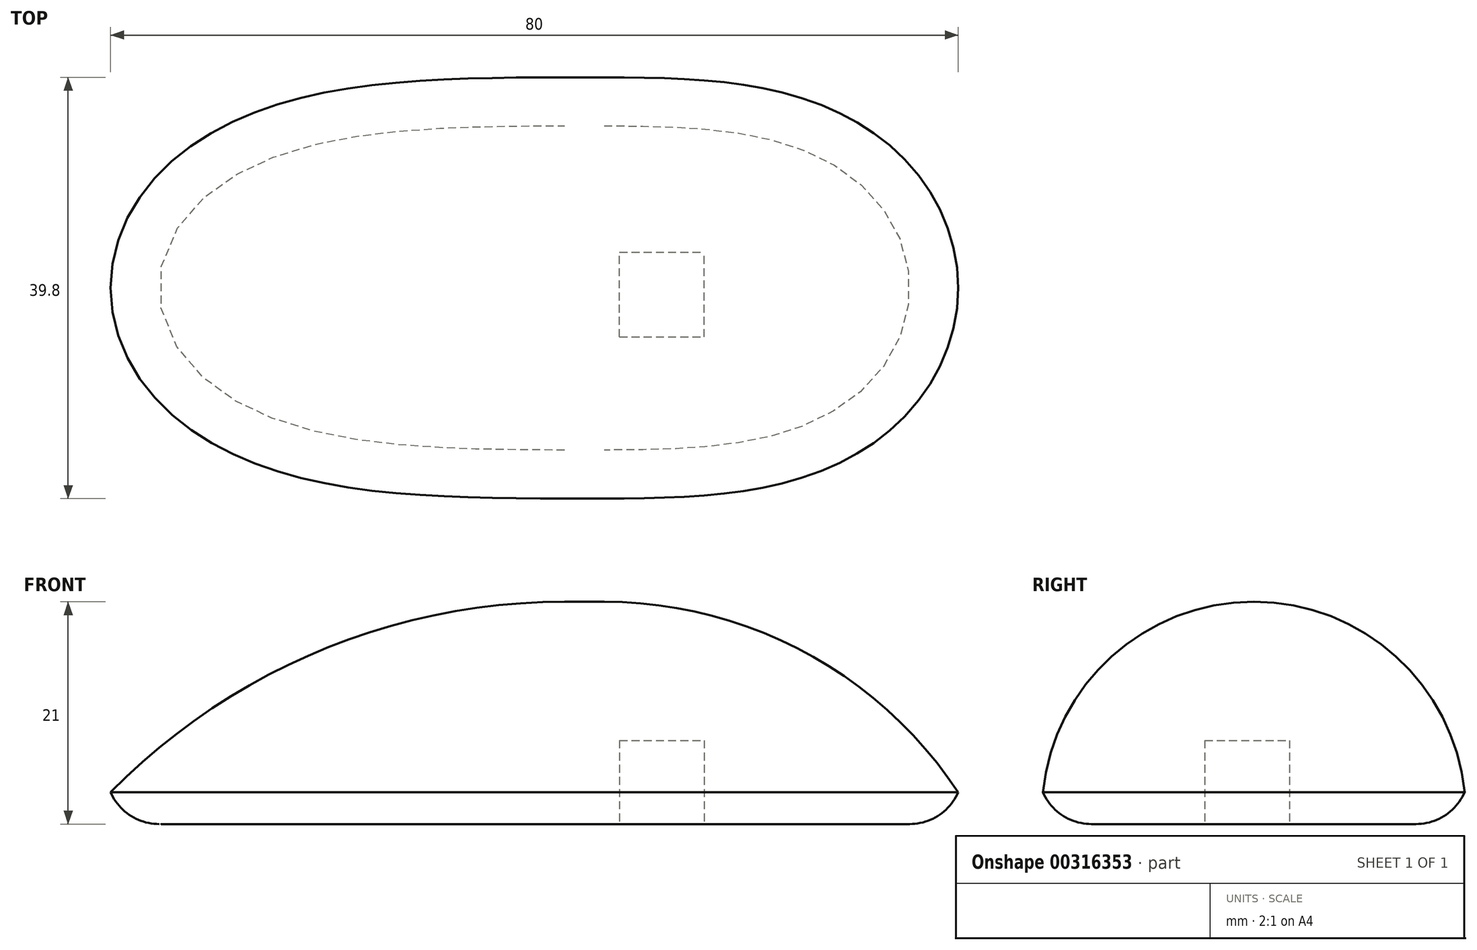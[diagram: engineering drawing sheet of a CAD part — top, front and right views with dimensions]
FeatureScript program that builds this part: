
annotation { "Feature Type Name" : "Feature", "Feature Type Description" : "" }
export const myFeature = defineFeature(function(context is Context, id is Id, definition is map)
    precondition{}
    {
        {
            var Q0;
            Q0=qCreatedBy(makeId("Front.planeOp"),FACE);
            var sketch = newSketch(context, id + "F0", { "sketchPlane" : qUnion([Q0])});
            skLineSegment(sketch, "E0.bottom", {"start": v(-60.2, 40.82) * mm, "end": v(19.8, 40.82) * mm});
            skLineSegment(sketch, "E0.top", {"start": v(-60.2, 22.82) * mm, "end": v(19.8, 22.82) * mm});
            skLineSegment(sketch, "E0.left", {"start": v(-60.2, 40.82) * mm, "end": v(-60.2, 22.82) * mm});
            skLineSegment(sketch, "E0.right", {"start": v(19.8, 40.82) * mm, "end": v(19.8, 22.82) * mm});
            skSolve(sketch);
        }
        {
            var Q0;
            Q0=makeQuery(id+"F0.imprint","IMPRINT",FACE,{"disambiguationData":[TD([[makeQuery(id+"F0.imprint","IMPRINT",EDGE,{"derivedFrom":sQuery(id+"F0.wireOp",EDGE,"E0.bottom")}),-1.0]])]});
            extrude(context, id + "F1", {"entities" : qUnion([Q0]), "depth" : 40 * mm});
        }
        {
            var Q0;
            Q0=makeQuery(id+"F1.opExtrude","SWEPT_EDGE",EDGE,{"disambiguationData":[OSD([sQuery(id+"F0.wireOp",EDGE,"E0.bottom"),sQuery(id+"F0.wireOp",EDGE,"E0.left")])]});
            fillet(context, id + "F2", {"entities" : qUnion([Q0]), "radius" : 60 * mm, "tangentPropagation" : true, "allowEdgeOverflow" : false});
        }
        {
            var Q0;
            Q0=makeQuery(id+"F1.opExtrude","SWEPT_EDGE",EDGE,{"disambiguationData":[OSD([sQuery(id+"F0.wireOp",EDGE,"E0.bottom"),sQuery(id+"F0.wireOp",EDGE,"E0.right")])]});
            fillet(context, id + "F3", {"entities" : qUnion([Q0]), "radius" : 40 * mm, "tangentPropagation" : true, "allowEdgeOverflow" : false});
        }
        {
            var Q0;
            {var subQ0=sQuery(id+"F0.wireOp",EDGE,"E0.left");var subQ1=sQuery(id+"F0.wireOp",EDGE,"E0.bottom");Q0=makeQuery(id+"F2.opFillet","BLEND_EDGE",EDGE,{"blendedFrom":[makeQuery(id+"F1.opExtrude","SWEPT_EDGE",EDGE,{"disambiguationData":[OSD([subQ1,subQ0])]}),makeQuery(id+"F1.opExtrude","CAP_FACE",FACE,{"disambiguationData":[OSD([subQ1,sQuery(id+"F0.wireOp",EDGE,"E0.top"),subQ0,sQuery(id+"F0.wireOp",EDGE,"E0.right")])],"isStart":false})],"blendedInto":[makeQuery(id+"F1.opExtrude","CAP_FACE",FACE,{"disambiguationData":[OSD([subQ1,sQuery(id+"F0.wireOp",EDGE,"E0.top"),subQ0,sQuery(id+"F0.wireOp",EDGE,"E0.right")])],"isStart":false})]});}
            var Q1;
            Q1=makeQuery(id+"F1.opExtrude","CAP_EDGE",EDGE,{"disambiguationData":[OSD([sQuery(id+"F0.wireOp",EDGE,"E0.bottom")])],"isStart":false});
            var Q2;
            {var subQ0=sQuery(id+"F0.wireOp",EDGE,"E0.right");var subQ1=sQuery(id+"F0.wireOp",EDGE,"E0.bottom");Q2=makeQuery(id+"F3.opFillet","BLEND_EDGE",EDGE,{"blendedFrom":[makeQuery(id+"F1.opExtrude","SWEPT_EDGE",EDGE,{"disambiguationData":[OSD([subQ1,subQ0])]}),makeQuery(id+"F1.opExtrude","CAP_FACE",FACE,{"disambiguationData":[OSD([subQ1,sQuery(id+"F0.wireOp",EDGE,"E0.top"),sQuery(id+"F0.wireOp",EDGE,"E0.left"),subQ0])],"isStart":false})],"blendedInto":[makeQuery(id+"F1.opExtrude","CAP_FACE",FACE,{"disambiguationData":[OSD([subQ1,sQuery(id+"F0.wireOp",EDGE,"E0.top"),sQuery(id+"F0.wireOp",EDGE,"E0.left"),subQ0])],"isStart":false})]});}
            fillet(context, id + "F4", {"entities" : qUnion([Q0, Q1, Q2]), "radius" : 20 * mm, "tangentPropagation" : true, "allowEdgeOverflow" : false});
        }
        {
            var Q0;
            {var subQ0=sQuery(id+"F0.wireOp",EDGE,"E0.right");var subQ1=sQuery(id+"F0.wireOp",EDGE,"E0.bottom");Q0=makeQuery(id+"F3.opFillet","BLEND_EDGE",EDGE,{"blendedFrom":[makeQuery(id+"F1.opExtrude","SWEPT_EDGE",EDGE,{"disambiguationData":[OSD([subQ1,subQ0])]}),makeQuery(id+"F1.opExtrude","CAP_FACE",FACE,{"disambiguationData":[OSD([subQ1,sQuery(id+"F0.wireOp",EDGE,"E0.top"),sQuery(id+"F0.wireOp",EDGE,"E0.left"),subQ0])],"isStart":true})],"blendedInto":[makeQuery(id+"F1.opExtrude","CAP_FACE",FACE,{"disambiguationData":[OSD([subQ1,sQuery(id+"F0.wireOp",EDGE,"E0.top"),sQuery(id+"F0.wireOp",EDGE,"E0.left"),subQ0])],"isStart":true})]});}
            var Q1;
            Q1=makeQuery(id+"F1.opExtrude","CAP_EDGE",EDGE,{"disambiguationData":[OSD([sQuery(id+"F0.wireOp",EDGE,"E0.bottom")])],"isStart":true});
            var Q2;
            {var subQ0=sQuery(id+"F0.wireOp",EDGE,"E0.left");var subQ1=sQuery(id+"F0.wireOp",EDGE,"E0.bottom");Q2=makeQuery(id+"F2.opFillet","BLEND_EDGE",EDGE,{"blendedFrom":[makeQuery(id+"F1.opExtrude","SWEPT_EDGE",EDGE,{"disambiguationData":[OSD([subQ1,subQ0])]}),makeQuery(id+"F1.opExtrude","CAP_FACE",FACE,{"disambiguationData":[OSD([subQ1,sQuery(id+"F0.wireOp",EDGE,"E0.top"),subQ0,sQuery(id+"F0.wireOp",EDGE,"E0.right")])],"isStart":true})],"blendedInto":[makeQuery(id+"F1.opExtrude","CAP_FACE",FACE,{"disambiguationData":[OSD([subQ1,sQuery(id+"F0.wireOp",EDGE,"E0.top"),subQ0,sQuery(id+"F0.wireOp",EDGE,"E0.right")])],"isStart":true})]});}
            fillet(context, id + "F5", {"entities" : qUnion([Q0, Q1, Q2]), "radius" : 20 * mm, "tangentPropagation" : true, "allowEdgeOverflow" : false});
        }
        {
            var Q0;
            Q0=makeQuery(id+"F1.opExtrude","SWEPT_FACE",FACE,{"disambiguationData":[OSD([sQuery(id+"F0.wireOp",EDGE,"E0.top")])]});
            extrude(context, id + "F6", {"entities" : qUnion([Q0]), "operationType" : NewBodyOperationType.ADD, "depth" : 3 * mm});
        }
        {
            var Q0;
            {var subQ0=sQuery(id+"F0.wireOp",EDGE,"E0.top");var subQ1=makeQuery(id+"F1.opExtrude","SWEPT_FACE",FACE,{"disambiguationData":[OSD([subQ0])]});var subQ2=sQuery(id+"F0.wireOp",EDGE,"E0.right");var subQ3=sQuery(id+"F0.wireOp",EDGE,"E0.left");var subQ4=sQuery(id+"F0.wireOp",EDGE,"E0.bottom");var subQ5=makeQuery(id+"F1.opExtrude","SWEPT_EDGE",EDGE,{"disambiguationData":[OSD([subQ4,subQ2])]});Q0=makeQuery(id+"F6.opExtrude","CAP_EDGE",EDGE,{"disambiguationData":[OSD([subQ4,subQ0,subQ3,subQ2]),TDD([makeQuery(id+"F4.opFillet","BLEND_EDGE",EDGE,{"blendedFrom":[makeQuery(id+"F3.opFillet","BLEND_EDGE",EDGE,{"blendedFrom":[subQ5,makeQuery(id+"F1.opExtrude","CAP_FACE",FACE,{"disambiguationData":[OSD([subQ4,subQ0,subQ3,subQ2])],"isStart":false})],"blendedInto":[makeQuery(id+"F1.opExtrude","CAP_FACE",FACE,{"disambiguationData":[OSD([subQ4,subQ0,subQ3,subQ2])],"isStart":false})]}),subQ1],"blendedInto":[subQ1]}),makeQuery(id+"F5.opFillet","BLEND_EDGE",EDGE,{"blendedFrom":[makeQuery(id+"F3.opFillet","BLEND_EDGE",EDGE,{"blendedFrom":[subQ5,makeQuery(id+"F1.opExtrude","CAP_FACE",FACE,{"disambiguationData":[OSD([subQ4,subQ0,subQ3,subQ2])],"isStart":true})],"blendedInto":[makeQuery(id+"F1.opExtrude","CAP_FACE",FACE,{"disambiguationData":[OSD([subQ4,subQ0,subQ3,subQ2])],"isStart":true})]}),subQ1],"blendedInto":[subQ1]})])],"isStart":false});}
            var Q1;
            {var subQ0=sQuery(id+"F0.wireOp",EDGE,"E0.top");var subQ1=makeQuery(id+"F1.opExtrude","SWEPT_FACE",FACE,{"disambiguationData":[OSD([subQ0])]});var subQ2=sQuery(id+"F0.wireOp",EDGE,"E0.right");var subQ3=sQuery(id+"F0.wireOp",EDGE,"E0.left");var subQ4=sQuery(id+"F0.wireOp",EDGE,"E0.bottom");var subQ5=makeQuery(id+"F1.opExtrude","SWEPT_EDGE",EDGE,{"disambiguationData":[OSD([subQ4,subQ3])]});Q1=makeQuery(id+"F6.opExtrude","CAP_EDGE",EDGE,{"disambiguationData":[OSD([subQ4,subQ0,subQ3,subQ2]),TDD([makeQuery(id+"F4.opFillet","BLEND_EDGE",EDGE,{"blendedFrom":[makeQuery(id+"F2.opFillet","BLEND_EDGE",EDGE,{"blendedFrom":[subQ5,makeQuery(id+"F1.opExtrude","CAP_FACE",FACE,{"disambiguationData":[OSD([subQ4,subQ0,subQ3,subQ2])],"isStart":false})],"blendedInto":[makeQuery(id+"F1.opExtrude","CAP_FACE",FACE,{"disambiguationData":[OSD([subQ4,subQ0,subQ3,subQ2])],"isStart":false})]}),subQ1],"blendedInto":[subQ1]}),makeQuery(id+"F5.opFillet","BLEND_EDGE",EDGE,{"blendedFrom":[makeQuery(id+"F2.opFillet","BLEND_EDGE",EDGE,{"blendedFrom":[subQ5,makeQuery(id+"F1.opExtrude","CAP_FACE",FACE,{"disambiguationData":[OSD([subQ4,subQ0,subQ3,subQ2])],"isStart":true})],"blendedInto":[makeQuery(id+"F1.opExtrude","CAP_FACE",FACE,{"disambiguationData":[OSD([subQ4,subQ0,subQ3,subQ2])],"isStart":true})]}),subQ1],"blendedInto":[subQ1]})])],"isStart":false});}
            fillet(context, id + "F7", {"entities" : qUnion([Q0, Q1]), "radius" : 5 * mm, "tangentPropagation" : true, "allowEdgeOverflow" : false});
        }
        {
            var Q0;
            Q0=makeQuery(id+"F6.opExtrude","CAP_FACE",FACE,{"disambiguationData":[OSD([sQuery(id+"F0.wireOp",EDGE,"E0.top")])],"isStart":false});
            var sketch = newSketch(context, id + "F8", { "sketchPlane" : qUnion([Q0])});
            skLineSegment(sketch, "E1.bottom", {"start": v(-12.17, 24.63) * mm, "end": v(-4.17, 24.63) * mm});
            skLineSegment(sketch, "E1.top", {"start": v(-12.17, 16.63) * mm, "end": v(-4.17, 16.63) * mm});
            skLineSegment(sketch, "E1.left", {"start": v(-12.17, 24.63) * mm, "end": v(-12.17, 16.63) * mm});
            skLineSegment(sketch, "E1.right", {"start": v(-4.17, 24.63) * mm, "end": v(-4.17, 16.63) * mm});
            skSolve(sketch);
        }
        {
            var Q0;
            Q0=makeQuery(id+"F8.imprint","IMPRINT",FACE,{"disambiguationData":[TD([[makeQuery(id+"F8.imprint","IMPRINT",EDGE,{"derivedFrom":sQuery(id+"F8.wireOp",EDGE,"E1.bottom")}),-1.0]])]});
            extrude(context, id + "F9", {"entities" : qUnion([Q0]), "operationType" : NewBodyOperationType.REMOVE, "oppositeDirection" : true, "depth" : 7.9 * mm});
        }
    });
